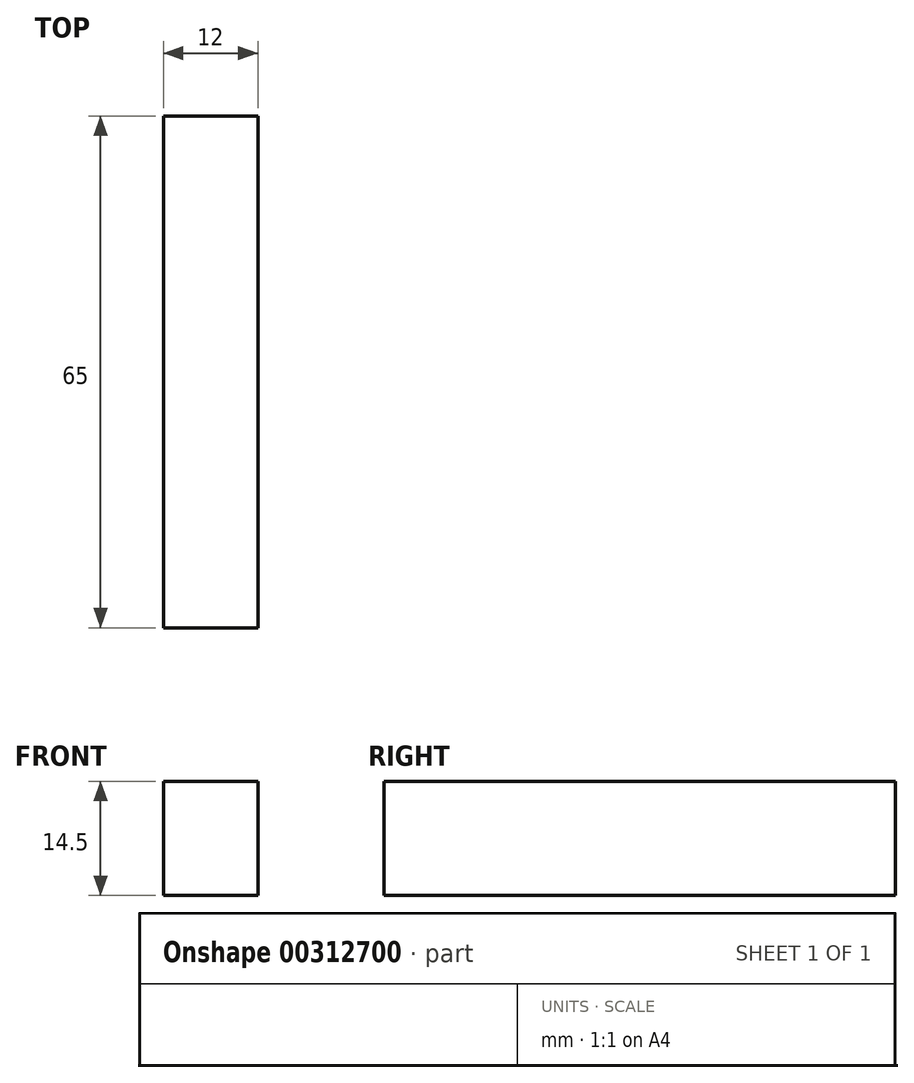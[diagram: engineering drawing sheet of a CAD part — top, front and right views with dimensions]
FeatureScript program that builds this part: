
annotation { "Feature Type Name" : "Feature", "Feature Type Description" : "" }
export const myFeature = defineFeature(function(context is Context, id is Id, definition is map)
    precondition{}
    {
        {
            var Q0;
            Q0=qCreatedBy(makeId("Top.planeOp"),FACE);
            var sketch = newSketch(context, id + "F0", { "sketchPlane" : qUnion([Q0])});
            skLineSegment(sketch, "E0.bottom", {"start": v(31.75, 41.44) * mm, "end": v(43.75, 41.44) * mm});
            skLineSegment(sketch, "E0.top", {"start": v(31.75, -23.56) * mm, "end": v(43.75, -23.56) * mm});
            skLineSegment(sketch, "E0.left", {"start": v(31.75, 41.44) * mm, "end": v(31.75, -23.56) * mm});
            skLineSegment(sketch, "E0.right", {"start": v(43.75, 41.44) * mm, "end": v(43.75, -23.56) * mm});
            skSolve(sketch);
        }
        {
            var Q0;
            Q0=makeQuery(id+"F0.imprint","IMPRINT",FACE,{"disambiguationData":[TD([[makeQuery(id+"F0.imprint","IMPRINT",EDGE,{"derivedFrom":sQuery(id+"F0.wireOp",EDGE,"E0.bottom")}),-1.0]])]});
            extrude(context, id + "F1", {"entities" : qUnion([Q0]), "depth" : 14.5 * mm});
        }
    });
